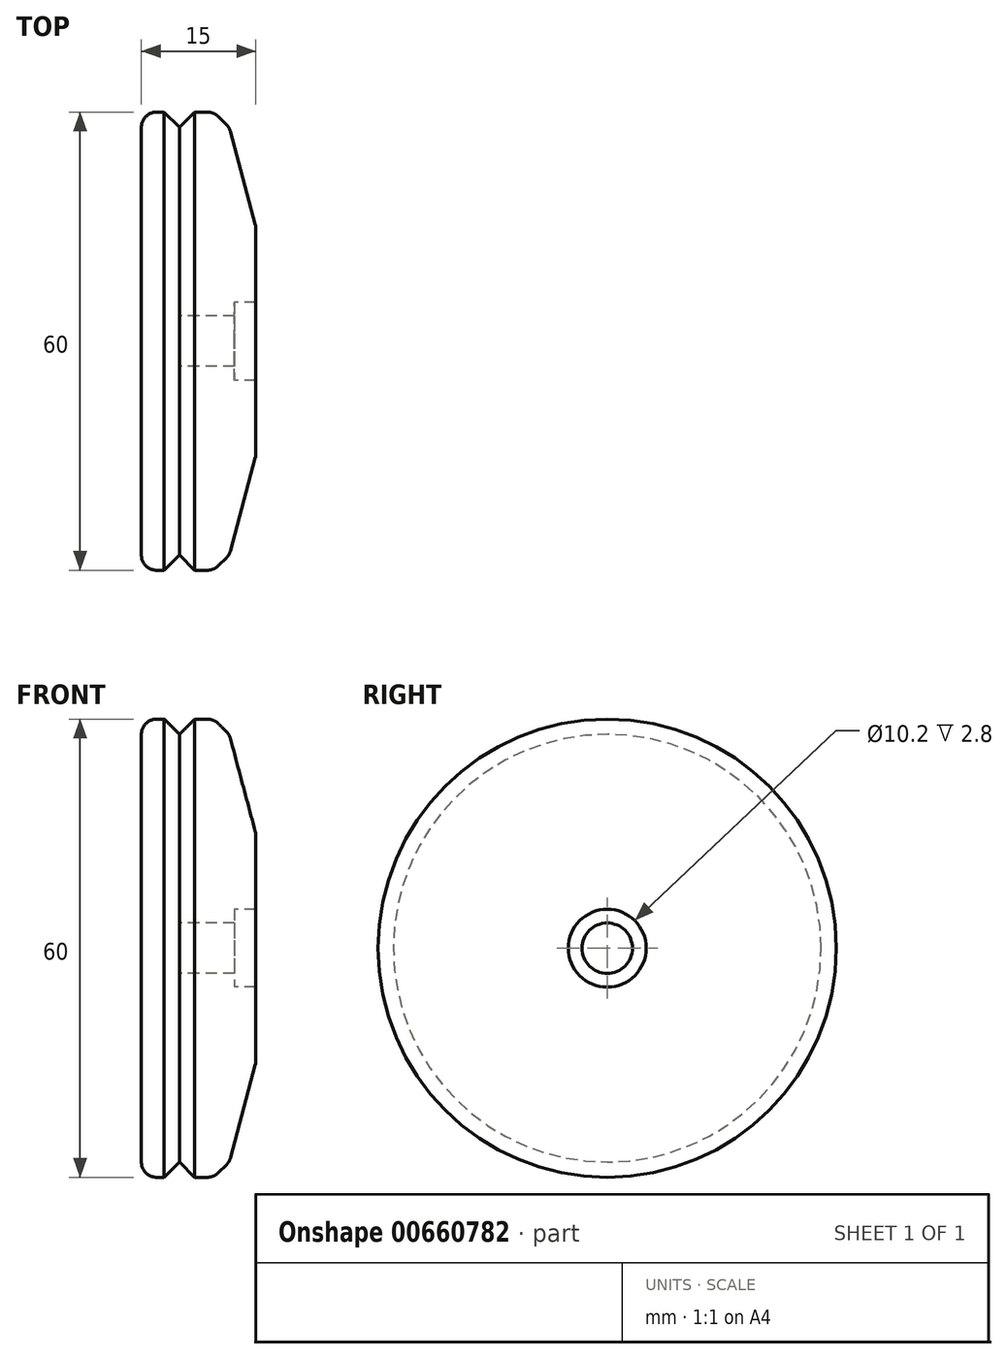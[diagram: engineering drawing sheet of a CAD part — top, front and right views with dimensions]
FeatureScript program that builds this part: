
annotation { "Feature Type Name" : "Feature", "Feature Type Description" : "" }
export const myFeature = defineFeature(function(context is Context, id is Id, definition is map)
    precondition{}
    {
        {
            var Q0;
            Q0=qCreatedBy(makeId("Front.planeOp"),FACE);
            var sketch = newSketch(context, id + "F0", { "sketchPlane" : qUnion([Q0])});
            skLineSegment(sketch, "E0", {"start": v(-0.07, 15.25) * mm, "end": v(-3.34, 27.46) * mm});
            skLineSegment(sketch, "E1", {"start": v(-3.86, 28.36) * mm, "end": v(-4.91, 29.41) * mm});
            skLineSegment(sketch, "E2", {"start": v(-6.33, 30) * mm, "end": v(-8, 30) * mm});
            skLineSegment(sketch, "E3", {"start": v(-12, 30) * mm, "end": v(-13, 30) * mm});
            skLineSegment(sketch, "E4", {"start": v(-38.77, 0) * mm, "end": v(37.35, 0) * mm});
            skLineSegment(sketch, "E5", {"start": v(-2.8, 5.1) * mm, "end": v(0, 5.1) * mm});
            skLineSegment(sketch, "E6", {"start": v(0, 5.1) * mm, "end": v(0, 14.74) * mm});
            skLineSegment(sketch, "E7", {"start": v(-10, 3.3) * mm, "end": v(-2.8, 3.3) * mm});
            skLineSegment(sketch, "E8", {"start": v(-2.8, 3.3) * mm, "end": v(-2.8, 5.1) * mm});
            skPoint(sketch, "E9.visualSharp", {"position": v(-15, 30) * mm});
            skArc(sketch, "E9.filletArc", {"start": v(-13, 30) * mm, "mid": v(-14.41, 29.41) * mm, "end": v(-15, 28) * mm});
            skPoint(sketch, "E10.visualSharp", {"position": v(-5.5, 30) * mm});
            skArc(sketch, "E10.filletArc", {"start": v(-4.91, 29.41) * mm, "mid": v(-5.56, 29.85) * mm, "end": v(-6.33, 30) * mm});
            skPoint(sketch, "E11.visualSharp", {"position": v(-3.48, 27.98) * mm});
            skArc(sketch, "E11.filletArc", {"start": v(-3.34, 27.46) * mm, "mid": v(-3.54, 27.94) * mm, "end": v(-3.86, 28.36) * mm});
            skPoint(sketch, "E12.visualSharp", {"position": v(0, 15) * mm});
            skArc(sketch, "E12.filletArc", {"start": v(0, 14.74) * mm, "mid": v(-0.02, 15) * mm, "end": v(-0.07, 15.25) * mm});
            skLineSegment(sketch, "E13", {"start": v(-12, 30) * mm, "end": v(-10, 28) * mm});
            skLineSegment(sketch, "E14", {"start": v(-10, 28) * mm, "end": v(-8, 30) * mm});
            skLineSegment(sketch, "E15", {"start": v(-15, 28) * mm, "end": v(-15, 0) * mm});
            skLineSegment(sketch, "E16", {"start": v(-15, 0) * mm, "end": v(-10, 0) * mm});
            skLineSegment(sketch, "E17", {"start": v(-10, 0) * mm, "end": v(-10, 3.3) * mm});
            skSolve(sketch);
        }
        {
            var Q0;
            Q0=makeQuery(id+"F0.imprint","IMPRINT",FACE,{"disambiguationData":[TD([[makeQuery(id+"F0.imprint","IMPRINT",EDGE,{"derivedFrom":sQuery(id+"F0.wireOp",EDGE,"E0")}),1.0]])]});
            var Q1;
            Q1=sQuery(id+"F0.wireOp",EDGE,"E4");
            revolve(context, id + "F1", {"entities" : qUnion([Q0]), "axis" : qUnion([Q1]), "revolveType" : RevolveType.FULL});
        }
    });
